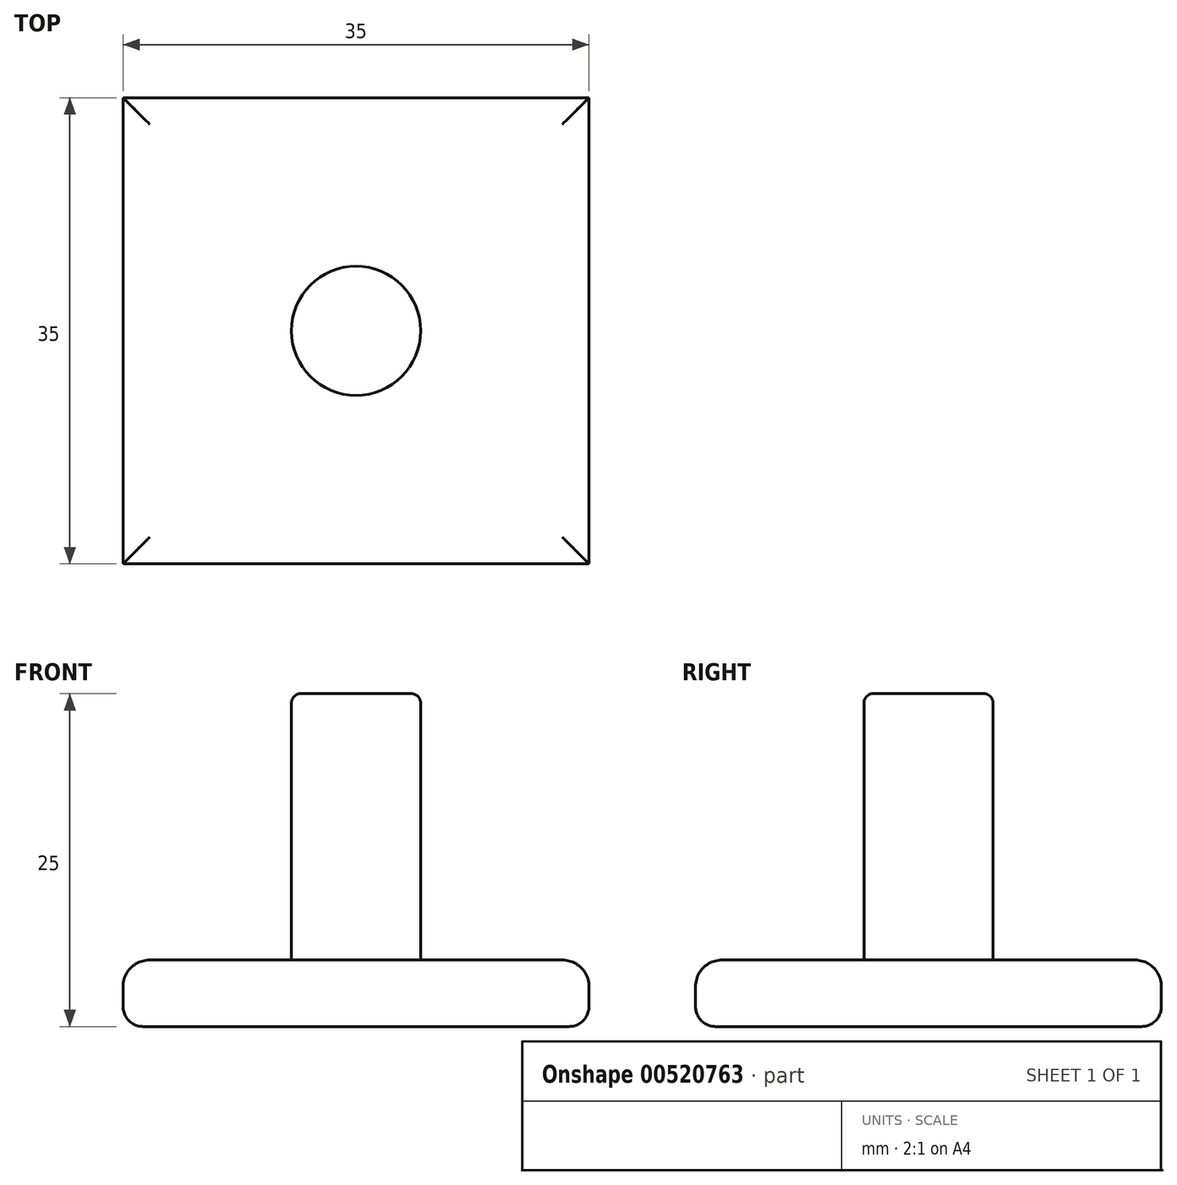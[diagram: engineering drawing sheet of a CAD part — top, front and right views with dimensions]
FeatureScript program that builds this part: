
annotation { "Feature Type Name" : "Feature", "Feature Type Description" : "" }
export const myFeature = defineFeature(function(context is Context, id is Id, definition is map)
    precondition{}
    {
        {
            var Q0;
            Q0=qCreatedBy(makeId("Top.planeOp"),FACE);
            var sketch = newSketch(context, id + "F0", { "sketchPlane" : qUnion([Q0])});
            skLineSegment(sketch, "E0.bottom", {"start": v(-17.5, 17.5) * mm, "end": v(17.5, 17.5) * mm});
            skLineSegment(sketch, "E0.top", {"start": v(-17.5, -17.5) * mm, "end": v(17.5, -17.5) * mm});
            skLineSegment(sketch, "E0.left", {"start": v(-17.5, 17.5) * mm, "end": v(-17.5, -17.5) * mm});
            skLineSegment(sketch, "E0.right", {"start": v(17.5, 17.5) * mm, "end": v(17.5, -17.5) * mm});
            skPoint(sketch, "E0.middle", {"position": v(0, 0) * mm});
            skPoint(sketch, "E1.orphan", {"position": v(0, 37.9) * mm});
            skPoint(sketch, "E2.orphan", {"position": v(-61.07, 0) * mm});
            skSolve(sketch);
        }
        {
            var Q0;
            Q0=qSketchRegion(id+"F0",true);
            extrude(context, id + "F1", {"entities" : qUnion([Q0]), "oppositeDirection" : true, "depth" : 5 * mm});
        }
        {
            var Q0;
            Q0=qCreatedBy(makeId("Top.planeOp"),FACE);
            var sketch = newSketch(context, id + "F2", { "sketchPlane" : qUnion([Q0])});
            skLineSegment(sketch, "E3", {"start": v(-47.54, 0) * mm, "end": v(45.98, 0) * mm, "construction": true});
            skLineSegment(sketch, "E4", {"start": v(45.98, 0) * mm, "end": v(46.2, 1.35) * mm, "construction": true});
            skLineSegment(sketch, "E5", {"start": v(0, 46.27) * mm, "end": v(0, -44.87) * mm, "construction": true});
            skPoint(sketch, "E6.center.orphan", {"position": v(-11.85, 0) * mm});
            skCircle(sketch, "E7", {"center": v(0, 0) * mm, "radius": 4.85 * mm});
            skSolve(sketch);
        }
        {
            var Q0;
            Q0=makeQuery(id+"F1.opExtrude","CAP_EDGE",EDGE,{"disambiguationData":[OSD([sQuery(id+"F0.wireOp",EDGE,"E0.top")])],"isStart":true});
            var Q1;
            Q1=makeQuery(id+"F1.opExtrude","CAP_EDGE",EDGE,{"disambiguationData":[OSD([sQuery(id+"F0.wireOp",EDGE,"E0.left")])],"isStart":true});
            var Q2;
            Q2=makeQuery(id+"F1.opExtrude","CAP_EDGE",EDGE,{"disambiguationData":[OSD([sQuery(id+"F0.wireOp",EDGE,"E0.bottom")])],"isStart":true});
            var Q3;
            Q3=makeQuery(id+"F1.opExtrude","CAP_EDGE",EDGE,{"disambiguationData":[OSD([sQuery(id+"F0.wireOp",EDGE,"E0.right")])],"isStart":true});
            var Q4;
            Q4=makeQuery(id+"FgNiEnVtFhhDMmq_1.opExtrude","CAP_EDGE",EDGE,{"disambiguationData":[OSD([sQuery(id+"F2.wireOp",EDGE,"dc8eaaea-79e6-4a7a-95c1-9608843dd01d0.MirrorC")])],"isStart":false});
            var Q5;
            Q5=makeQuery(id+"FgNiEnVtFhhDMmq_1.opExtrude","CAP_EDGE",EDGE,{"disambiguationData":[OSD([sQuery(id+"F2.wireOp",EDGE,"E6")])],"isStart":false});
            fillet(context, id + "F3", {"entities" : qUnion([Q0, Q1, Q2, Q3, Q4, Q5]), "radius" : 2 * mm, "tangentPropagation" : true, "allowEdgeOverflow" : false});
        }
        {
            var Q0;
            Q0=makeQuery(id+"F1.opExtrude","CAP_FACE",FACE,{"disambiguationData":[OSD([sQuery(id+"F0.wireOp",EDGE,"E0.bottom"),sQuery(id+"F0.wireOp",EDGE,"E0.top"),sQuery(id+"F0.wireOp",EDGE,"E0.left"),sQuery(id+"F0.wireOp",EDGE,"E0.right")])],"isStart":false});
            fillet(context, id + "F4", {"entities" : qUnion([Q0]), "radius" : 1.5 * mm, "tangentPropagation" : true, "allowEdgeOverflow" : false});
        }
        {
            var Q0;
            Q0 = qSketchRegion(id + "F2", true);
            extrude(context, id + "F5", {"entities" : qUnion([Q0]), "operationType" : NewBodyOperationType.ADD, "depth" : 20 * mm, "offsetDistance" : 25 * mm});
        }
        {
            var Q0;
            Q0=makeQuery(id+"F5.opExtrude","CAP_FACE",FACE,{"disambiguationData":[OSD([sQuery(id+"F2.wireOp",EDGE,"E7")])],"isStart":false});
            fillet(context, id + "F6", {"entities" : qUnion([Q0]), "radius" : .7 * mm, "tangentPropagation" : true, "allowEdgeOverflow" : false});
        }
    });
